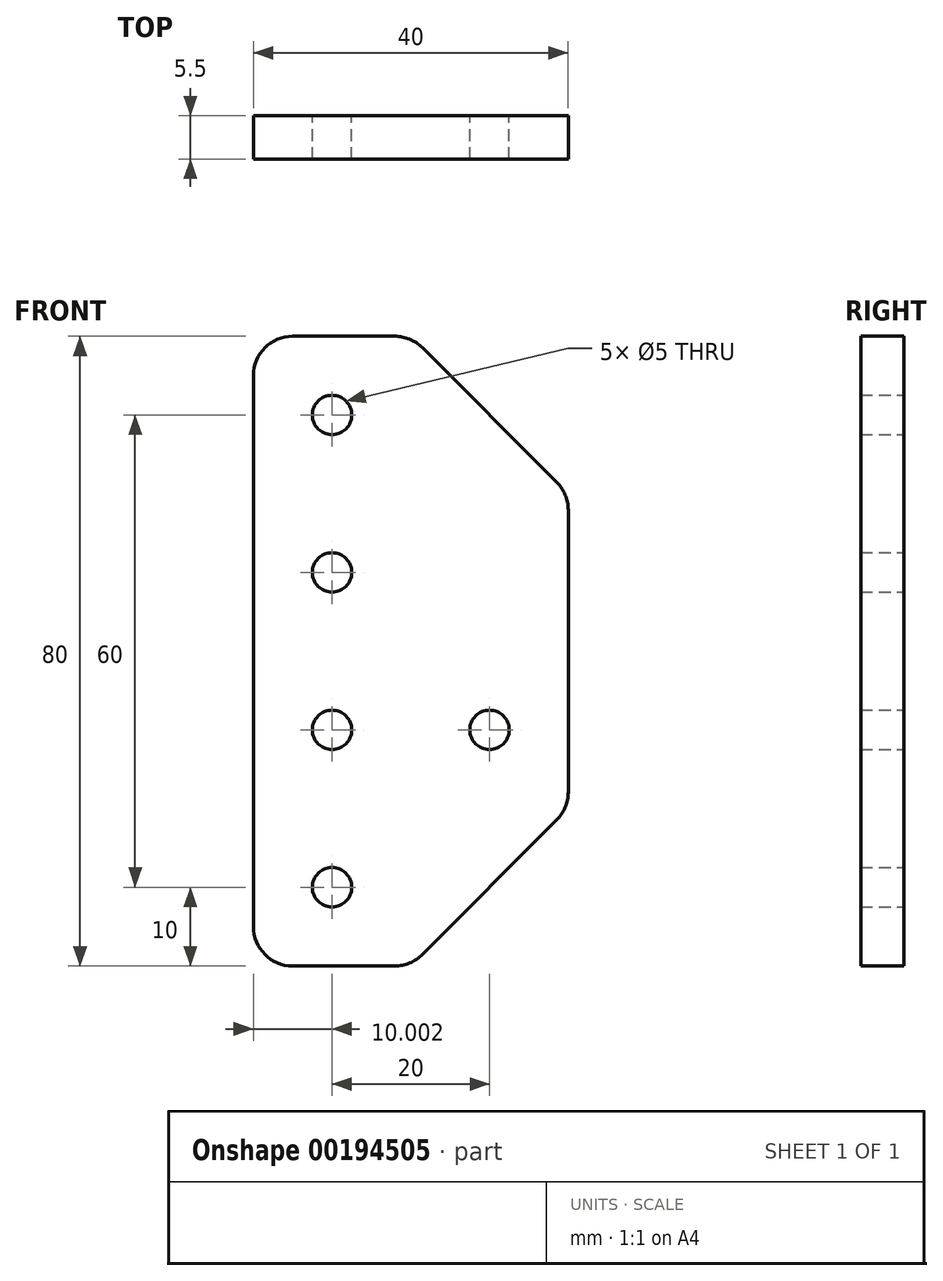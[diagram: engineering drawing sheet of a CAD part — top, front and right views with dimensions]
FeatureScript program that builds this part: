
annotation { "Feature Type Name" : "Feature", "Feature Type Description" : "" }
export const myFeature = defineFeature(function(context is Context, id is Id, definition is map)
    precondition{}
    {
        {
            var Q0;
            Q0=qCreatedBy(makeId("Front.planeOp"),FACE);
            var sketch = newSketch(context, id + "F0", { "sketchPlane" : qUnion([Q0])});
            skLineSegment(sketch, "E0.bottom", {"start": v(-11.66, 20) * mm, "end": v(3.34, 20) * mm});
            skLineSegment(sketch, "E0.top", {"start": v(-11.66, -20) * mm, "end": v(1.27, -20) * mm});
            skLineSegment(sketch, "E0.left", {"start": v(-16.66, 15) * mm, "end": v(-16.66, -15) * mm});
            skLineSegment(sketch, "E1.left", {"start": v(-16.66, 15) * mm, "end": v(-16.66, 0) * mm});
            skLineSegment(sketch, "E1.right", {"start": v(23.34, 15) * mm, "end": v(23.34, 2.07) * mm});
            skLineSegment(sketch, "E2", {"start": v(4.8, -18.54) * mm, "end": v(21.88, -1.46) * mm});
            skPoint(sketch, "E3.visualSharp", {"position": v(-16.66, 20) * mm});
            skPoint(sketch, "E4.visualSharp", {"position": v(-16.66, -20) * mm});
            skArc(sketch, "E4.filletArc", {"start": v(-16.66, -15) * mm, "mid": v(-15.2, -18.54) * mm, "end": v(-11.66, -20) * mm});
            skPoint(sketch, "E5.visualSharp", {"position": v(23.34, 20) * mm});
            skPoint(sketch, "E6.visualSharp", {"position": v(23.34, 0) * mm});
            skArc(sketch, "E6.filletArc", {"start": v(21.88, -1.46) * mm, "mid": v(22.96, 0.16) * mm, "end": v(23.34, 2.07) * mm});
            skPoint(sketch, "E7.visualSharp", {"position": v(3.34, -20) * mm});
            skArc(sketch, "E7.filletArc", {"start": v(1.27, -20) * mm, "mid": v(3.18, -19.62) * mm, "end": v(4.8, -18.54) * mm});
            skPoint(sketch, "E8", {"position": v(-5.2, -20) * mm});
            skPoint(sketch, "E9", {"position": v(23.34, 8.54) * mm});
            skPoint(sketch, "E10", {"position": v(-6.66, 0) * mm});
            skPoint(sketch, "E11", {"position": v(3.34, 10) * mm});
            skPoint(sketch, "E12", {"position": v(-6.66, 20) * mm});
            skPoint(sketch, "E13", {"position": v(-16.66, 10) * mm});
            skCircle(sketch, "E14", {"center": v(-6.66, 10) * mm, "radius": 2.5 * mm});
            skCircle(sketch, "E15", {"center": v(13.34, 10) * mm, "radius": 2.5 * mm});
            skCircle(sketch, "E16", {"center": v(-6.66, -10) * mm, "radius": 2.5 * mm});
            skCircle(sketch, "E17", {"center": v(3.34, 10) * mm, "radius": 2.5 * mm});
            skCircle(sketch, "E18", {"center": v(-6.66, 0) * mm, "radius": 2.5 * mm});
            skArc(sketch, "E19.MirrorCS", {"start": v(1.27, 60) * mm, "mid": v(3.18, 59.62) * mm, "end": v(4.8, 58.54) * mm});
            skArc(sketch, "E20.MirrorCS", {"start": v(21.88, 41.46) * mm, "mid": v(22.96, 39.84) * mm, "end": v(23.34, 37.93) * mm});
            skPoint(sketch, "E21.MirrorP", {"position": v(23.34, 31.46) * mm});
            skPoint(sketch, "E22.MirrorP", {"position": v(3.34, 30) * mm});
            skPoint(sketch, "E23.MirrorP", {"position": v(-16.66, 30) * mm});
            skArc(sketch, "E24.MirrorCS", {"start": v(-16.66, 55) * mm, "mid": v(-15.2, 58.54) * mm, "end": v(-11.66, 60) * mm});
            skLineSegment(sketch, "E25.MirrorCS", {"start": v(4.8, 58.54) * mm, "end": v(21.88, 41.46) * mm});
            skLineSegment(sketch, "E26.MirrorCS", {"start": v(23.34, 25) * mm, "end": v(23.34, 37.93) * mm});
            skLineSegment(sketch, "E27.MirrorCS", {"start": v(-16.66, 25) * mm, "end": v(-16.66, 40) * mm});
            skPoint(sketch, "E28.MirrorP", {"position": v(23.34, 40) * mm});
            skLineSegment(sketch, "E29.MirrorCS", {"start": v(-16.66, 25) * mm, "end": v(-16.66, 55) * mm});
            skPoint(sketch, "E30.MirrorP", {"position": v(3.34, 60) * mm});
            skLineSegment(sketch, "E31.MirrorCS", {"start": v(-11.66, 60) * mm, "end": v(1.27, 60) * mm});
            skPoint(sketch, "E32.MirrorP", {"position": v(-5.2, 60) * mm});
            skCircle(sketch, "E33.MirrorC", {"center": v(-6.66, 50) * mm, "radius": 2.5 * mm});
            skPoint(sketch, "E34.MirrorP", {"position": v(-6.66, 40) * mm});
            skCircle(sketch, "E35.MirrorC", {"center": v(-6.66, 30) * mm, "radius": 2.5 * mm});
            skPoint(sketch, "E36.MirrorP", {"position": v(-16.66, 60) * mm});
            skLineSegment(sketch, "E37", {"start": v(-16.66, 25) * mm, "end": v(-16.66, 15) * mm});
            skLineSegment(sketch, "E38", {"start": v(23.34, 25) * mm, "end": v(23.34, 15) * mm});
            skSolve(sketch);
        }
        {
            var Q0;
            Q0=makeQuery(id+"F0.imprint","IMPRINT",FACE,{"disambiguationData":[TD([[makeQuery(id+"F0.imprint","IMPRINT",EDGE,{"derivedFrom":sQuery(id+"F0.wireOp",EDGE,"E0.top")}),1.0]])]});
            var Q1;
            Q1=makeQuery(id+"F0.imprint","IMPRINT",FACE,{"disambiguationData":[TD([[makeQuery(id+"F0.imprint","IMPRINT",EDGE,{"derivedFrom":sQuery(id+"F0.wireOp",EDGE,"E18")}),1.0]])]});
            var Q2;
            Q2=makeQuery(id+"F0.imprint","IMPRINT",FACE,{"disambiguationData":[TD([[makeQuery(id+"F0.imprint","IMPRINT",EDGE,{"derivedFrom":sQuery(id+"F0.wireOp",EDGE,"E17")}),1.0]])]});
            extrude(context, id + "F1", {"entities" : qUnion([Q0, Q1, Q2]), "depth" : 5.5 * mm, "offsetDistance" : 25.4 * mm});
        }
    });
